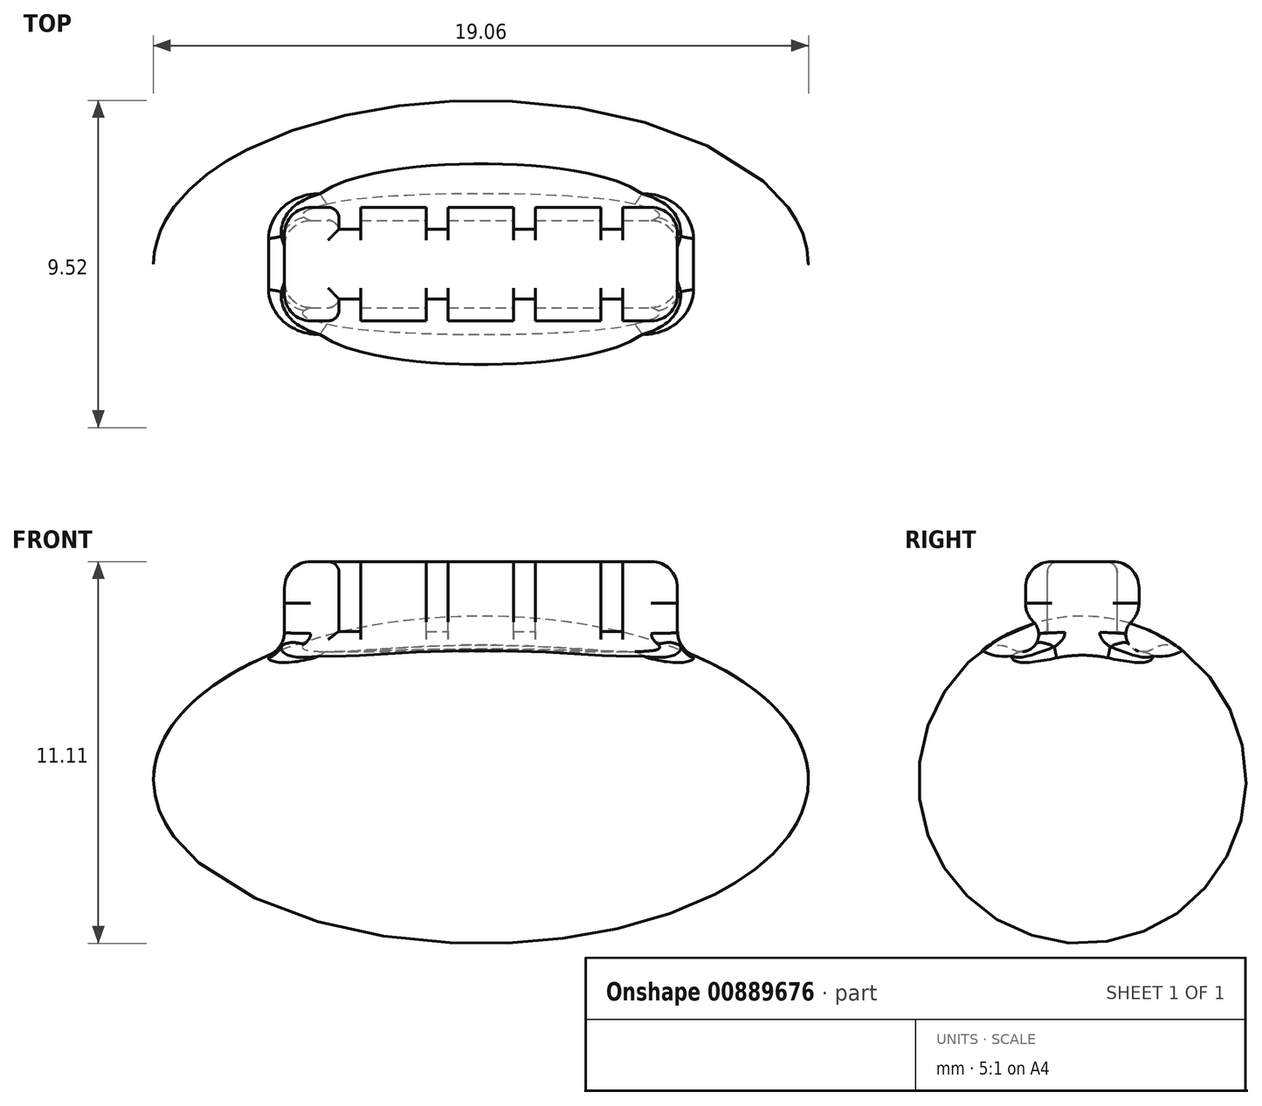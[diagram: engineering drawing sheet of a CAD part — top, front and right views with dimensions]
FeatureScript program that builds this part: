
annotation { "Feature Type Name" : "Feature", "Feature Type Description" : "" }
export const myFeature = defineFeature(function(context is Context, id is Id, definition is map)
    precondition{}
    {
        {
            var Q0;
            Q0=qCreatedBy(makeId("Front.planeOp"),FACE);
            var sketch = newSketch(context, id + "F0", { "sketchPlane" : qUnion([Q0])});
            skEllipticalArc(sketch, "E0", {});
            skLineSegment(sketch, "E1", {"start": v(0, 4.76) * mm, "end": v(0, 0) * mm});
            skEllipticalArc(sketch, "E2.MirrorCS", {});
            skLineSegment(sketch, "E3", {"start": v(-9.52, 0) * mm, "end": v(9.52, 0) * mm});
            skPoint(sketch, "E4.orphan", {"position": v(0, -4.76) * mm});
            const initialGuessF0  = {"E0": [0, 0, -1, 0, 0.009525, 0.0047625, 3.141592653589793, 4.71238898038469], "E2.MirrorCS": [0, 0, 1, 0, 0.009525, 0.0047625, 1.5707963267948966, 3.141592653589793]};
            skSetInitialGuess(sketch, initialGuessF0);
            skSolve(sketch);
        }
        {
            var Q0;
            Q0 = qSketchRegion(id + "F0", true);
            var Q1;
            Q1=sQuery(id+"F0.wireOp",EDGE,"E3");
            revolve(context, id + "F1", {"surfaceOperationType" : NewSurfaceOperationType.NEW, "entities" : qUnion([Q0]), "axis" : qUnion([Q1]), "revolveType" : RevolveType.FULL});
        }
        {
            var Q0;
            Q0=qCreatedBy(makeId("Top.planeOp"),FACE);
            var sketch = newSketch(context, id + "F2", { "sketchPlane" : qUnion([Q0])});
            skLineSegment(sketch, "E5.bottom", {"start": v(-5.72, 1.65) * mm, "end": v(5.72, 1.65) * mm});
            skLineSegment(sketch, "E5.top", {"start": v(-5.72, -1.65) * mm, "end": v(5.72, -1.65) * mm});
            skLineSegment(sketch, "E5.left", {"start": v(-5.72, 1.65) * mm, "end": v(-5.72, -1.65) * mm});
            skLineSegment(sketch, "E5.right", {"start": v(5.72, 1.65) * mm, "end": v(5.72, -1.65) * mm});
            skLineSegment(sketch, "E6", {"start": v(-5.71, 0) * mm, "end": v(5.71, 0) * mm, "construction": true});
            skSolve(sketch);
        }
        {
            var Q0;
            Q0 = qSketchRegion(id + "F2", true);
            extrude(context, id + "F3", {"entities" : qUnion([Q0]), "operationType" : NewBodyOperationType.ADD, "depth" : 6.35 * mm, "offsetDistance" : 25.4 * mm});
        }
        {
            var Q0;
            Q0=makeQuery(id+"F3.opExtrude","CAP_EDGE",EDGE,{"disambiguationData":[OSD([sQuery(id+"F2.wireOp",EDGE,"E5.top")])],"isStart":false});
            var Q1;
            Q1=makeQuery(id+"F3.opExtrude","CAP_EDGE",EDGE,{"disambiguationData":[OSD([sQuery(id+"F2.wireOp",EDGE,"E5.bottom")])],"isStart":false});
            var Q2;
            Q2=makeQuery(id+"F3.opExtrude","SWEPT_FACE",FACE,{"disambiguationData":[OSD([sQuery(id+"F2.wireOp",EDGE,"E5.right")])]});
            var Q3;
            Q3=makeQuery(id+"F3.opExtrude","SWEPT_FACE",FACE,{"disambiguationData":[OSD([sQuery(id+"F2.wireOp",EDGE,"E5.left")])]});
            fillet(context, id + "F4", {"entities" : qUnion([Q0, Q1, Q2, Q3]), "radius" : 0.76 * mm, "tangentPropagation" : true, "allowEdgeOverflow" : false});
        }
        {
            var Q0;
            Q0=makeQuery(id+"F3.opExtrude","SWEPT_FACE",FACE,{"disambiguationData":[OSD([sQuery(id+"F2.wireOp",EDGE,"E5.right")])]});
            var sketch = newSketch(context, id + "F5", { "sketchPlane" : qUnion([Q0])});
            skCircle(sketch, "E7", {"center": v(1.78, 4.23) * mm, "radius": 0.5 * mm});
            skLineSegment(sketch, "E8", {"start": v(0, 4.33) * mm, "end": v(1.78, 4.23) * mm, "construction": true});
            skPoint(sketch, "E9", {"position": v(0, 4.33) * mm});
            skLineSegment(sketch, "E10", {"start": v(0, 4.33) * mm, "end": v(0, 4.7) * mm, "construction": true});
            skCircle(sketch, "E11.MirrorC", {"center": v(-1.78, 4.23) * mm, "radius": 0.5 * mm});
            skSolve(sketch);
        }
        {
            var Q0;
            Q0 = qSketchRegion(id + "F5", true);
            var Q1;
            Q1=makeQuery(id+"F3.opExtrude","SWEPT_FACE",FACE,{"disambiguationData":[OSD([sQuery(id+"F2.wireOp",EDGE,"E5.left")])]});
            extrude(context, id + "F6", {"entities" : qUnion([Q0, Q1]), "operationType" : NewBodyOperationType.REMOVE, "oppositeDirection" : true, "depth" : 25.4 * mm, "offsetDistance" : 25.4 * mm});
        }
        {
            var Q0;
            Q0=makeQuery(id+"F6.boolean.opBoolean","INTERSECT",EDGE,{"derivedFrom":[makeQuery(id+"F1.opRevolve","SWEPT_FACE",FACE,{"disambiguationData":[OSD([sQuery(id+"F0.wireOp",EDGE,"E0"),sQuery(id+"F0.wireOp",EDGE,"E2.MirrorCS")])]}),makeQuery(id+"F6.opExtrude","SWEPT_FACE",FACE,{"disambiguationData":[OSD([sQuery(id+"F5.wireOp",EDGE,"E11.MirrorC")])]})]});
            var Q1;
            Q1=makeQuery(id+"F6.boolean.opBoolean","INTERSECT",EDGE,{"derivedFrom":[makeQuery(id+"F1.opRevolve","SWEPT_FACE",FACE,{"disambiguationData":[OSD([sQuery(id+"F0.wireOp",EDGE,"E0"),sQuery(id+"F0.wireOp",EDGE,"E2.MirrorCS")])]}),makeQuery(id+"F6.opExtrude","SWEPT_FACE",FACE,{"disambiguationData":[OSD([sQuery(id+"F5.wireOp",EDGE,"E7")])]})]});
            fillet(context, id + "F7", {"entities" : qUnion([Q0, Q1]), "radius" : 0.76 * mm, "tangentPropagation" : true, "allowEdgeOverflow" : false});
        }
        {
            var Q0;
            Q0=makeQuery(id+"F3.opExtrude","CAP_FACE",FACE,{"disambiguationData":[OSD([sQuery(id+"F2.wireOp",EDGE,"E5.bottom"),sQuery(id+"F2.wireOp",EDGE,"E5.top"),sQuery(id+"F2.wireOp",EDGE,"E5.left"),sQuery(id+"F2.wireOp",EDGE,"E5.right")])],"isStart":false});
            var sketch = newSketch(context, id + "F8", { "sketchPlane" : qUnion([Q0])});
            skLineSegment(sketch, "E12.bottom", {"start": v(-4.13, 1.65) * mm, "end": v(-3.5, 1.65) * mm});
            skLineSegment(sketch, "E12.top", {"start": v(-4.13, 1.02) * mm, "end": v(-3.5, 1.02) * mm});
            skLineSegment(sketch, "E12.left", {"start": v(-4.13, 1.65) * mm, "end": v(-4.13, 1.02) * mm});
            skLineSegment(sketch, "E12.right", {"start": v(-3.5, 1.65) * mm, "end": v(-3.5, 1.02) * mm});
            skLineSegment(sketch, "E13.bottom", {"start": v(-1.59, 1.65) * mm, "end": v(-0.95, 1.65) * mm});
            skLineSegment(sketch, "E13.top", {"start": v(-1.59, 1.02) * mm, "end": v(-0.95, 1.02) * mm});
            skLineSegment(sketch, "E13.left", {"start": v(-1.59, 1.65) * mm, "end": v(-1.59, 1.02) * mm});
            skLineSegment(sketch, "E13.right", {"start": v(-0.95, 1.65) * mm, "end": v(-0.95, 1.02) * mm});
            skLineSegment(sketch, "E14.bottom", {"start": v(0.95, 1.65) * mm, "end": v(1.59, 1.65) * mm});
            skLineSegment(sketch, "E14.top", {"start": v(0.95, 1.02) * mm, "end": v(1.59, 1.02) * mm});
            skLineSegment(sketch, "E14.left", {"start": v(0.95, 1.65) * mm, "end": v(0.95, 1.02) * mm});
            skLineSegment(sketch, "E14.right", {"start": v(1.59, 1.65) * mm, "end": v(1.59, 1.02) * mm});
            skLineSegment(sketch, "E15.bottom", {"start": v(3.5, 1.65) * mm, "end": v(4.13, 1.65) * mm});
            skLineSegment(sketch, "E15.top", {"start": v(3.5, 1.02) * mm, "end": v(4.13, 1.02) * mm});
            skLineSegment(sketch, "E15.left", {"start": v(3.5, 1.65) * mm, "end": v(3.5, 1.02) * mm});
            skLineSegment(sketch, "E15.right", {"start": v(4.13, 1.65) * mm, "end": v(4.13, 1.02) * mm});
            skLineSegment(sketch, "E16", {"start": v(-4.13, 1.02) * mm, "end": v(-4.95, 0.89) * mm, "construction": true});
            skLineSegment(sketch, "E17", {"start": v(4.13, 1.02) * mm, "end": v(4.95, 0.89) * mm, "construction": true});
            skLineSegment(sketch, "E18", {"start": v(-4.95, 0) * mm, "end": v(4.95, 0) * mm, "construction": true});
            skLineSegment(sketch, "E19.MirrorCS", {"start": v(-4.13, -1.65) * mm, "end": v(-3.5, -1.65) * mm});
            skLineSegment(sketch, "E20.MirrorCS", {"start": v(4.13, -1.65) * mm, "end": v(4.13, -1.02) * mm});
            skLineSegment(sketch, "E21.MirrorCS", {"start": v(-1.59, -1.65) * mm, "end": v(-1.59, -1.02) * mm});
            skLineSegment(sketch, "E22.MirrorCS", {"start": v(-1.59, -1.65) * mm, "end": v(-0.95, -1.65) * mm});
            skLineSegment(sketch, "E23.MirrorCS", {"start": v(0.95, -1.65) * mm, "end": v(1.59, -1.65) * mm});
            skLineSegment(sketch, "E24.MirrorCS", {"start": v(3.5, -1.65) * mm, "end": v(3.5, -1.02) * mm});
            skLineSegment(sketch, "E25.MirrorCS", {"start": v(-3.5, -1.65) * mm, "end": v(-3.5, -1.02) * mm});
            skLineSegment(sketch, "E26.MirrorCS", {"start": v(-4.13, -1.65) * mm, "end": v(-4.13, -1.02) * mm});
            skLineSegment(sketch, "E27.MirrorCS", {"start": v(-4.13, -1.02) * mm, "end": v(-3.5, -1.02) * mm});
            skLineSegment(sketch, "E28.MirrorCS", {"start": v(-0.95, -1.65) * mm, "end": v(-0.95, -1.02) * mm});
            skLineSegment(sketch, "E29.MirrorCS", {"start": v(0.95, -1.65) * mm, "end": v(0.95, -1.02) * mm});
            skLineSegment(sketch, "E30.MirrorCS", {"start": v(3.5, -1.02) * mm, "end": v(4.13, -1.02) * mm});
            skLineSegment(sketch, "E31.MirrorCS", {"start": v(0.95, -1.02) * mm, "end": v(1.59, -1.02) * mm});
            skLineSegment(sketch, "E32.MirrorCS", {"start": v(1.59, -1.65) * mm, "end": v(1.59, -1.02) * mm});
            skLineSegment(sketch, "E33.MirrorCS", {"start": v(-1.59, -1.02) * mm, "end": v(-0.95, -1.02) * mm});
            skLineSegment(sketch, "E34.MirrorCS", {"start": v(3.5, -1.65) * mm, "end": v(4.13, -1.65) * mm});
            skSolve(sketch);
        }
        {
            var Q0;
            Q0 = qSketchRegion(id + "F8", true);
            extrude(context, id + "F9", {"entities" : qUnion([Q0]), "operationType" : NewBodyOperationType.REMOVE, "oppositeDirection" : true, "depth" : 2.03 * mm, "offsetDistance" : 25.4 * mm});
        }
        {
            var Q0;
            Q0=makeQuery(id+"F9.boolean.opBoolean","INTERSECT",EDGE,{"derivedFrom":[makeQuery(id+"F6.boolean.opBoolean","COPY",FACE,{"derivedFrom":makeQuery(id+"F6.opExtrude","SWEPT_FACE",FACE,{"disambiguationData":[OSD([sQuery(id+"F5.wireOp",EDGE,"E11.MirrorC")])]})}),makeQuery(id+"F9.opExtrude","CAP_FACE",FACE,{"disambiguationData":[OSD([sQuery(id+"F8.wireOp",EDGE,"E19.MirrorCS"),sQuery(id+"F8.wireOp",EDGE,"E25.MirrorCS"),sQuery(id+"F8.wireOp",EDGE,"E26.MirrorCS"),sQuery(id+"F8.wireOp",EDGE,"E27.MirrorCS")])],"isStart":false})]});
            var Q1;
            Q1=makeQuery(id+"F9.boolean.opBoolean","INTERSECT",EDGE,{"derivedFrom":[makeQuery(id+"F4.opFillet","BLEND_FACE",FACE,{"disambiguationData":[OSD([sQuery(id+"F2.wireOp",EDGE,"E5.top")])]}),makeQuery(id+"F9.opExtrude","SWEPT_FACE",FACE,{"disambiguationData":[OSD([sQuery(id+"F8.wireOp",EDGE,"E27.MirrorCS")])]})]});
            var Q2;
            Q2=makeQuery(id+"F9.boolean.opBoolean","INTERSECT",EDGE,{"derivedFrom":[makeQuery(id+"F4.opFillet","BLEND_FACE",FACE,{"disambiguationData":[OSD([sQuery(id+"F2.wireOp",EDGE,"E5.top")])]}),makeQuery(id+"F9.opExtrude","SWEPT_FACE",FACE,{"disambiguationData":[OSD([sQuery(id+"F8.wireOp",EDGE,"E33.MirrorCS")])]})]});
            var Q3;
            Q3=makeQuery(id+"F9.boolean.opBoolean","INTERSECT",EDGE,{"derivedFrom":[makeQuery(id+"F6.boolean.opBoolean","COPY",FACE,{"derivedFrom":makeQuery(id+"F6.opExtrude","SWEPT_FACE",FACE,{"disambiguationData":[OSD([sQuery(id+"F5.wireOp",EDGE,"E11.MirrorC")])]})}),makeQuery(id+"F9.opExtrude","CAP_FACE",FACE,{"disambiguationData":[OSD([sQuery(id+"F8.wireOp",EDGE,"E21.MirrorCS"),sQuery(id+"F8.wireOp",EDGE,"E22.MirrorCS"),sQuery(id+"F8.wireOp",EDGE,"E28.MirrorCS"),sQuery(id+"F8.wireOp",EDGE,"E33.MirrorCS")])],"isStart":false})]});
            var Q4;
            Q4=makeQuery(id+"F9.boolean.opBoolean","INTERSECT",EDGE,{"derivedFrom":[makeQuery(id+"F6.boolean.opBoolean","COPY",FACE,{"derivedFrom":makeQuery(id+"F6.opExtrude","SWEPT_FACE",FACE,{"disambiguationData":[OSD([sQuery(id+"F5.wireOp",EDGE,"E11.MirrorC")])]})}),makeQuery(id+"F9.opExtrude","CAP_FACE",FACE,{"disambiguationData":[OSD([sQuery(id+"F8.wireOp",EDGE,"E23.MirrorCS"),sQuery(id+"F8.wireOp",EDGE,"E29.MirrorCS"),sQuery(id+"F8.wireOp",EDGE,"E31.MirrorCS"),sQuery(id+"F8.wireOp",EDGE,"E32.MirrorCS")])],"isStart":false})]});
            var Q5;
            Q5=makeQuery(id+"F9.boolean.opBoolean","INTERSECT",EDGE,{"derivedFrom":[makeQuery(id+"F4.opFillet","BLEND_FACE",FACE,{"disambiguationData":[OSD([sQuery(id+"F2.wireOp",EDGE,"E5.top")])]}),makeQuery(id+"F9.opExtrude","SWEPT_FACE",FACE,{"disambiguationData":[OSD([sQuery(id+"F8.wireOp",EDGE,"E31.MirrorCS")])]})]});
            var Q6;
            Q6=makeQuery(id+"F9.boolean.opBoolean","INTERSECT",EDGE,{"derivedFrom":[makeQuery(id+"F3.opExtrude","SWEPT_FACE",FACE,{"disambiguationData":[OSD([sQuery(id+"F2.wireOp",EDGE,"E5.top")])]}),makeQuery(id+"F9.opExtrude","SWEPT_FACE",FACE,{"disambiguationData":[OSD([sQuery(id+"F8.wireOp",EDGE,"E29.MirrorCS")])]})]});
            var Q7;
            Q7=makeQuery(id+"F9.boolean.opBoolean","INTERSECT",EDGE,{"derivedFrom":[makeQuery(id+"F3.opExtrude","SWEPT_FACE",FACE,{"disambiguationData":[OSD([sQuery(id+"F2.wireOp",EDGE,"E5.top")])]}),makeQuery(id+"F9.opExtrude","SWEPT_FACE",FACE,{"disambiguationData":[OSD([sQuery(id+"F8.wireOp",EDGE,"E28.MirrorCS")])]})]});
            var Q8;
            Q8=makeQuery(id+"F9.boolean.opBoolean","INTERSECT",EDGE,{"derivedFrom":[makeQuery(id+"F3.opExtrude","SWEPT_FACE",FACE,{"disambiguationData":[OSD([sQuery(id+"F2.wireOp",EDGE,"E5.top")])]}),makeQuery(id+"F9.opExtrude","SWEPT_FACE",FACE,{"disambiguationData":[OSD([sQuery(id+"F8.wireOp",EDGE,"E21.MirrorCS")])]})]});
            var Q9;
            Q9=makeQuery(id+"F9.boolean.opBoolean","INTERSECT",EDGE,{"derivedFrom":[makeQuery(id+"F3.opExtrude","SWEPT_FACE",FACE,{"disambiguationData":[OSD([sQuery(id+"F2.wireOp",EDGE,"E5.top")])]}),makeQuery(id+"F9.opExtrude","SWEPT_FACE",FACE,{"disambiguationData":[OSD([sQuery(id+"F8.wireOp",EDGE,"E25.MirrorCS")])]})]});
            var Q10;
            {var subQ0=sQuery(id+"F5.wireOp",EDGE,"E11.MirrorC");var subQ1=sQuery(id+"F2.wireOp",EDGE,"E5.top");Q10=makeQuery(id+"F9.boolean.opBoolean","INTERSECT",EDGE,{"derivedFrom":[makeQuery(id+"F7.opFillet","BLEND_FACE",FACE,{"disambiguationData":[OSD([subQ1,subQ0]),TDD([makeQuery(id+"F6.boolean.opBoolean","INTERSECT",EDGE,{"disambiguationData":[OD(0.0)],"derivedFrom":[makeQuery(id+"F3.opExtrude","SWEPT_FACE",FACE,{"disambiguationData":[OSD([subQ1])]}),makeQuery(id+"F6.opExtrude","SWEPT_FACE",FACE,{"disambiguationData":[OSD([subQ0])]})]})])]}),makeQuery(id+"F9.opExtrude","SWEPT_FACE",FACE,{"disambiguationData":[OSD([sQuery(id+"F8.wireOp",EDGE,"E26.MirrorCS")])]})]});}
            var Q11;
            Q11=makeQuery(id+"F9.boolean.opBoolean","INTERSECT",EDGE,{"derivedFrom":[makeQuery(id+"F3.opExtrude","SWEPT_FACE",FACE,{"disambiguationData":[OSD([sQuery(id+"F2.wireOp",EDGE,"E5.top")])]}),makeQuery(id+"F9.opExtrude","SWEPT_FACE",FACE,{"disambiguationData":[OSD([sQuery(id+"F8.wireOp",EDGE,"E32.MirrorCS")])]})]});
            var Q12;
            Q12=makeQuery(id+"F9.boolean.opBoolean","INTERSECT",EDGE,{"derivedFrom":[makeQuery(id+"F4.opFillet","BLEND_FACE",FACE,{"disambiguationData":[OSD([sQuery(id+"F2.wireOp",EDGE,"E5.top")])]}),makeQuery(id+"F9.opExtrude","SWEPT_FACE",FACE,{"disambiguationData":[OSD([sQuery(id+"F8.wireOp",EDGE,"E30.MirrorCS")])]})]});
            var Q13;
            Q13=makeQuery(id+"F9.boolean.opBoolean","INTERSECT",EDGE,{"derivedFrom":[makeQuery(id+"F6.boolean.opBoolean","COPY",FACE,{"derivedFrom":makeQuery(id+"F6.opExtrude","SWEPT_FACE",FACE,{"disambiguationData":[OSD([sQuery(id+"F5.wireOp",EDGE,"E11.MirrorC")])]})}),makeQuery(id+"F9.opExtrude","CAP_FACE",FACE,{"disambiguationData":[OSD([sQuery(id+"F8.wireOp",EDGE,"E20.MirrorCS"),sQuery(id+"F8.wireOp",EDGE,"E24.MirrorCS"),sQuery(id+"F8.wireOp",EDGE,"E30.MirrorCS"),sQuery(id+"F8.wireOp",EDGE,"E34.MirrorCS")])],"isStart":false})]});
            var Q14;
            Q14=makeQuery(id+"F9.boolean.opBoolean","INTERSECT",EDGE,{"derivedFrom":[makeQuery(id+"F3.opExtrude","SWEPT_FACE",FACE,{"disambiguationData":[OSD([sQuery(id+"F2.wireOp",EDGE,"E5.top")])]}),makeQuery(id+"F9.opExtrude","SWEPT_FACE",FACE,{"disambiguationData":[OSD([sQuery(id+"F8.wireOp",EDGE,"E24.MirrorCS")])]})]});
            var Q15;
            Q15=makeQuery(id+"F9.boolean.opBoolean","INTERSECT",EDGE,{"derivedFrom":[makeQuery(id+"F3.opExtrude","SWEPT_FACE",FACE,{"disambiguationData":[OSD([sQuery(id+"F2.wireOp",EDGE,"E5.top")])]}),makeQuery(id+"F9.opExtrude","SWEPT_FACE",FACE,{"disambiguationData":[OSD([sQuery(id+"F8.wireOp",EDGE,"E20.MirrorCS")])]})]});
            var Q16;
            Q16=makeQuery(id+"F9.boolean.opBoolean","INTERSECT",EDGE,{"derivedFrom":[makeQuery(id+"F6.boolean.opBoolean","COPY",FACE,{"derivedFrom":makeQuery(id+"F6.opExtrude","SWEPT_FACE",FACE,{"disambiguationData":[OSD([sQuery(id+"F5.wireOp",EDGE,"E7")])]})}),makeQuery(id+"F9.opExtrude","CAP_FACE",FACE,{"disambiguationData":[OSD([sQuery(id+"F8.wireOp",EDGE,"E15.bottom"),sQuery(id+"F8.wireOp",EDGE,"E15.top"),sQuery(id+"F8.wireOp",EDGE,"E15.left"),sQuery(id+"F8.wireOp",EDGE,"E15.right")])],"isStart":false})]});
            var Q17;
            Q17=makeQuery(id+"F9.boolean.opBoolean","INTERSECT",EDGE,{"derivedFrom":[makeQuery(id+"F4.opFillet","BLEND_FACE",FACE,{"disambiguationData":[OSD([sQuery(id+"F2.wireOp",EDGE,"E5.bottom")])]}),makeQuery(id+"F9.opExtrude","SWEPT_FACE",FACE,{"disambiguationData":[OSD([sQuery(id+"F8.wireOp",EDGE,"E15.top")])]})]});
            var Q18;
            Q18=makeQuery(id+"F9.boolean.opBoolean","INTERSECT",EDGE,{"derivedFrom":[makeQuery(id+"F3.opExtrude","SWEPT_FACE",FACE,{"disambiguationData":[OSD([sQuery(id+"F2.wireOp",EDGE,"E5.bottom")])]}),makeQuery(id+"F9.opExtrude","SWEPT_FACE",FACE,{"disambiguationData":[OSD([sQuery(id+"F8.wireOp",EDGE,"E15.right")])]})]});
            var Q19;
            Q19=makeQuery(id+"F9.boolean.opBoolean","INTERSECT",EDGE,{"derivedFrom":[makeQuery(id+"F3.opExtrude","SWEPT_FACE",FACE,{"disambiguationData":[OSD([sQuery(id+"F2.wireOp",EDGE,"E5.bottom")])]}),makeQuery(id+"F9.opExtrude","SWEPT_FACE",FACE,{"disambiguationData":[OSD([sQuery(id+"F8.wireOp",EDGE,"E15.left")])]})]});
            var Q20;
            Q20=makeQuery(id+"F9.boolean.opBoolean","INTERSECT",EDGE,{"derivedFrom":[makeQuery(id+"F3.opExtrude","SWEPT_FACE",FACE,{"disambiguationData":[OSD([sQuery(id+"F2.wireOp",EDGE,"E5.bottom")])]}),makeQuery(id+"F9.opExtrude","SWEPT_FACE",FACE,{"disambiguationData":[OSD([sQuery(id+"F8.wireOp",EDGE,"E14.right")])]})]});
            var Q21;
            Q21=makeQuery(id+"F9.boolean.opBoolean","INTERSECT",EDGE,{"derivedFrom":[makeQuery(id+"F6.boolean.opBoolean","COPY",FACE,{"derivedFrom":makeQuery(id+"F6.opExtrude","SWEPT_FACE",FACE,{"disambiguationData":[OSD([sQuery(id+"F5.wireOp",EDGE,"E7")])]})}),makeQuery(id+"F9.opExtrude","CAP_FACE",FACE,{"disambiguationData":[OSD([sQuery(id+"F8.wireOp",EDGE,"E14.bottom"),sQuery(id+"F8.wireOp",EDGE,"E14.top"),sQuery(id+"F8.wireOp",EDGE,"E14.left"),sQuery(id+"F8.wireOp",EDGE,"E14.right")])],"isStart":false})]});
            var Q22;
            Q22=makeQuery(id+"F9.boolean.opBoolean","INTERSECT",EDGE,{"derivedFrom":[makeQuery(id+"F4.opFillet","BLEND_FACE",FACE,{"disambiguationData":[OSD([sQuery(id+"F2.wireOp",EDGE,"E5.bottom")])]}),makeQuery(id+"F9.opExtrude","SWEPT_FACE",FACE,{"disambiguationData":[OSD([sQuery(id+"F8.wireOp",EDGE,"E14.top")])]})]});
            var Q23;
            Q23=makeQuery(id+"F9.boolean.opBoolean","INTERSECT",EDGE,{"derivedFrom":[makeQuery(id+"F3.opExtrude","SWEPT_FACE",FACE,{"disambiguationData":[OSD([sQuery(id+"F2.wireOp",EDGE,"E5.bottom")])]}),makeQuery(id+"F9.opExtrude","SWEPT_FACE",FACE,{"disambiguationData":[OSD([sQuery(id+"F8.wireOp",EDGE,"E14.left")])]})]});
            var Q24;
            Q24=makeQuery(id+"F9.boolean.opBoolean","INTERSECT",EDGE,{"derivedFrom":[makeQuery(id+"F6.boolean.opBoolean","COPY",FACE,{"derivedFrom":makeQuery(id+"F6.opExtrude","SWEPT_FACE",FACE,{"disambiguationData":[OSD([sQuery(id+"F5.wireOp",EDGE,"E7")])]})}),makeQuery(id+"F9.opExtrude","CAP_FACE",FACE,{"disambiguationData":[OSD([sQuery(id+"F8.wireOp",EDGE,"E13.bottom"),sQuery(id+"F8.wireOp",EDGE,"E13.top"),sQuery(id+"F8.wireOp",EDGE,"E13.left"),sQuery(id+"F8.wireOp",EDGE,"E13.right")])],"isStart":false})]});
            var Q25;
            Q25=makeQuery(id+"F9.boolean.opBoolean","INTERSECT",EDGE,{"derivedFrom":[makeQuery(id+"F4.opFillet","BLEND_FACE",FACE,{"disambiguationData":[OSD([sQuery(id+"F2.wireOp",EDGE,"E5.bottom")])]}),makeQuery(id+"F9.opExtrude","SWEPT_FACE",FACE,{"disambiguationData":[OSD([sQuery(id+"F8.wireOp",EDGE,"E13.top")])]})]});
            var Q26;
            Q26=makeQuery(id+"F9.boolean.opBoolean","INTERSECT",EDGE,{"derivedFrom":[makeQuery(id+"F3.opExtrude","SWEPT_FACE",FACE,{"disambiguationData":[OSD([sQuery(id+"F2.wireOp",EDGE,"E5.bottom")])]}),makeQuery(id+"F9.opExtrude","SWEPT_FACE",FACE,{"disambiguationData":[OSD([sQuery(id+"F8.wireOp",EDGE,"E13.right")])]})]});
            var Q27;
            Q27=makeQuery(id+"F9.boolean.opBoolean","INTERSECT",EDGE,{"derivedFrom":[makeQuery(id+"F3.opExtrude","SWEPT_FACE",FACE,{"disambiguationData":[OSD([sQuery(id+"F2.wireOp",EDGE,"E5.bottom")])]}),makeQuery(id+"F9.opExtrude","SWEPT_FACE",FACE,{"disambiguationData":[OSD([sQuery(id+"F8.wireOp",EDGE,"E13.left")])]})]});
            var Q28;
            Q28=makeQuery(id+"F9.boolean.opBoolean","INTERSECT",EDGE,{"derivedFrom":[makeQuery(id+"F3.opExtrude","SWEPT_FACE",FACE,{"disambiguationData":[OSD([sQuery(id+"F2.wireOp",EDGE,"E5.bottom")])]}),makeQuery(id+"F9.opExtrude","SWEPT_FACE",FACE,{"disambiguationData":[OSD([sQuery(id+"F8.wireOp",EDGE,"E12.right")])]})]});
            var Q29;
            Q29=makeQuery(id+"F9.boolean.opBoolean","INTERSECT",EDGE,{"derivedFrom":[makeQuery(id+"F4.opFillet","BLEND_FACE",FACE,{"disambiguationData":[OSD([sQuery(id+"F2.wireOp",EDGE,"E5.bottom")])]}),makeQuery(id+"F9.opExtrude","SWEPT_FACE",FACE,{"disambiguationData":[OSD([sQuery(id+"F8.wireOp",EDGE,"E12.top")])]})]});
            var Q30;
            Q30=makeQuery(id+"F9.boolean.opBoolean","INTERSECT",EDGE,{"derivedFrom":[makeQuery(id+"F6.boolean.opBoolean","COPY",FACE,{"derivedFrom":makeQuery(id+"F6.opExtrude","SWEPT_FACE",FACE,{"disambiguationData":[OSD([sQuery(id+"F5.wireOp",EDGE,"E7")])]})}),makeQuery(id+"F9.opExtrude","CAP_FACE",FACE,{"disambiguationData":[OSD([sQuery(id+"F8.wireOp",EDGE,"E12.bottom"),sQuery(id+"F8.wireOp",EDGE,"E12.top"),sQuery(id+"F8.wireOp",EDGE,"E12.left"),sQuery(id+"F8.wireOp",EDGE,"E12.right")])],"isStart":false})]});
            var Q31;
            Q31=makeQuery(id+"F9.boolean.opBoolean","INTERSECT",EDGE,{"derivedFrom":[makeQuery(id+"F3.opExtrude","SWEPT_FACE",FACE,{"disambiguationData":[OSD([sQuery(id+"F2.wireOp",EDGE,"E5.bottom")])]}),makeQuery(id+"F9.opExtrude","SWEPT_FACE",FACE,{"disambiguationData":[OSD([sQuery(id+"F8.wireOp",EDGE,"E12.left")])]})]});
            fillet(context, id + "F10", {"entities" : qUnion([Q0, Q1, Q2, Q3, Q4, Q5, Q6, Q7, Q8, Q9, Q10, Q11, Q12, Q13, Q14, Q15, Q16, Q17, Q18, Q19, Q20, Q21, Q22, Q23, Q24, Q25, Q26, Q27, Q28, Q29, Q30, Q31]), "radius" : 0.32 * mm, "tangentPropagation" : true, "allowEdgeOverflow" : false});
        }
    });
